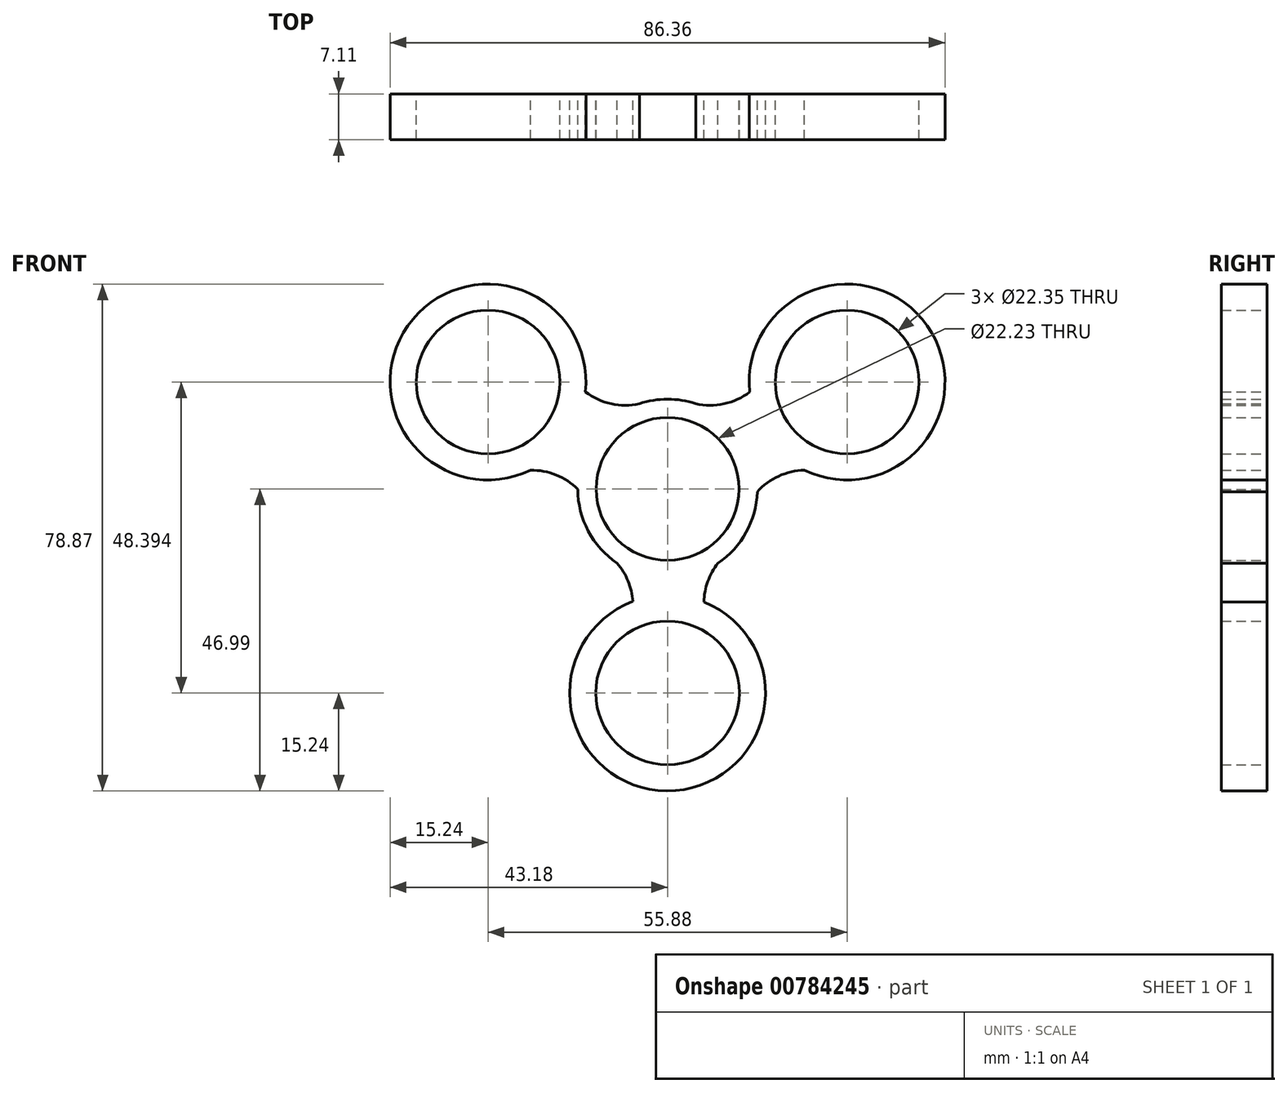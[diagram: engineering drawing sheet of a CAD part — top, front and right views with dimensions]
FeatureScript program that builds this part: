
annotation { "Feature Type Name" : "Feature", "Feature Type Description" : "" }
export const myFeature = defineFeature(function(context is Context, id is Id, definition is map)
    precondition{}
    {
        {
            var Q0;
            Q0=qCreatedBy(makeId("Front.planeOp"),FACE);
            var sketch = newSketch(context, id + "F0", { "sketchPlane" : qUnion([Q0])});
            skCircle(sketch, "E0", {"center": v(0, 0) * mm, "radius": 11.11 * mm});
            skCircle(sketch, "E1", {"center": v(0, 0) * mm, "radius": 13.97 * mm});
            skCircle(sketch, "E2", {"center": v(0, -31.75) * mm, "radius": 11.18 * mm});
            skCircle(sketch, "E3", {"center": v(0, -31.75) * mm, "radius": 15.24 * mm});
            skArc(sketch, "E4", {"start": v(7.85, -11.55) * mm, "mid": v(6.26, -14.4) * mm, "end": v(5.65, -17.6) * mm});
            skArc(sketch, "E5.MirrorCS", {"start": v(-7.85, -11.55) * mm, "mid": v(-6.15, -14.33) * mm, "end": v(-5.4, -17.5) * mm});
            skCircle(sketch, "E6", {"center": v(-27.94, 16.64) * mm, "radius": 11.18 * mm});
            skCircle(sketch, "E7", {"center": v(-27.94, 16.64) * mm, "radius": 15.24 * mm});
            skArc(sketch, "E8", {"start": v(-13.97, -0.05) * mm, "mid": v(-17.35, 2.18) * mm, "end": v(-21.32, 2.92) * mm});
            skArc(sketch, "E9.MirrorCS", {"start": v(-3.27, 13.58) * mm, "mid": v(-8.22, 13.15) * mm, "end": v(-12.78, 15.09) * mm});
            skArc(sketch, "E10.MirrorCS", {"start": v(3.27, 13.58) * mm, "mid": v(8.21, 13.14) * mm, "end": v(12.78, 15.08) * mm});
            skArc(sketch, "E11.MirrorCS", {"start": v(13.96, -0.46) * mm, "mid": v(17.29, 2) * mm, "end": v(21.31, 2.92) * mm});
            skCircle(sketch, "E12.MirrorC", {"center": v(27.94, 16.64) * mm, "radius": 15.24 * mm});
            skCircle(sketch, "E13.MirrorC", {"center": v(27.94, 16.64) * mm, "radius": 11.18 * mm});
            skCircle(sketch, "E14", {"center": v(0, 0) * mm, "radius": 11.05 * mm});
            skSolve(sketch);
        }
        {
            var Q0;
            Q0 = qSketchRegion(id + "F0", true);
            extrude(context, id + "F1", {"entities" : qUnion([Q0]), "depth" : 7.11 * mm, "offsetDistance" : 25.4 * mm});
        }
    });
